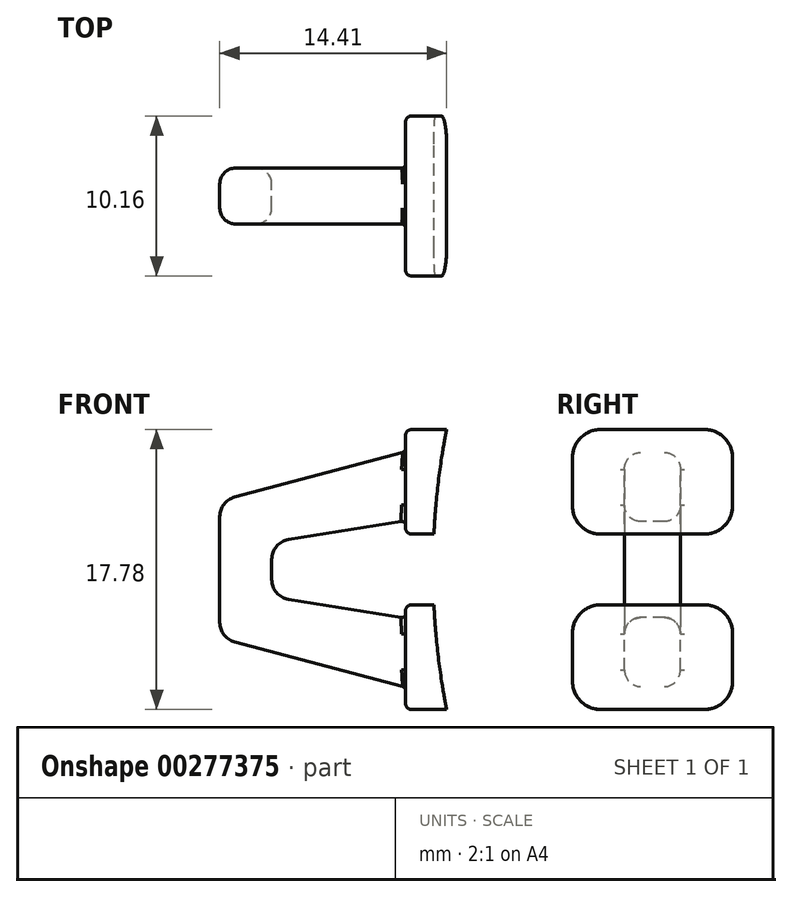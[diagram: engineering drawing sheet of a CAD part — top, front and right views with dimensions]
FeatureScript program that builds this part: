
annotation { "Feature Type Name" : "Feature", "Feature Type Description" : "" }
export const myFeature = defineFeature(function(context is Context, id is Id, definition is map)
    precondition{}
    {
        {
            var Q0;
            Q0=qCreatedBy(makeId("Front.planeOp"),FACE);
            var sketch = newSketch(context, id + "F0", { "sketchPlane" : qUnion([Q0])});
            skLineSegment(sketch, "E0", {"start": v(-28.89, -8.9) * mm, "end": v(-31.5, -8.9) * mm});
            skLineSegment(sketch, "E1", {"start": v(-31.5, -8.9) * mm, "end": v(-31.5, -7.48) * mm});
            skLineSegment(sketch, "E2.trimOffspring", {"start": v(-31.5, -3.1) * mm, "end": v(-31.5, -2.25) * mm});
            skLineSegment(sketch, "E3.MirrorCS", {"start": v(-31.5, 3.1) * mm, "end": v(-31.5, 2.25) * mm});
            skLineSegment(sketch, "E4.MirrorCS", {"start": v(-31.5, 8.9) * mm, "end": v(-31.5, 7.48) * mm});
            skLineSegment(sketch, "E5.MirrorCS", {"start": v(-28.89, 8.89) * mm, "end": v(-31.5, 8.89) * mm});
            skPoint(sketch, "E6.orphan", {"position": v(-29.04, 2.25) * mm});
            skPoint(sketch, "E7.orphan", {"position": v(-29.04, 8.9) * mm});
            skPoint(sketch, "E8.end.orphan", {"position": v(-29.04, -8.9) * mm});
            skPoint(sketch, "E8.start.orphan", {"position": v(-29.04, -2.25) * mm});
            skPoint(sketch, "E9.MirrorCS.end.orphan", {"position": v(-37.85, 0) * mm});
            skPoint(sketch, "E10.MirrorCS.end.orphan", {"position": v(-35.7, 0) * mm});
            skLineSegment(sketch, "E11", {"start": v(-31.5, -7.48) * mm, "end": v(-43.3, -4.35) * mm});
            skLineSegment(sketch, "E12", {"start": v(-43.3, -4.35) * mm, "end": v(-43.3, 0) * mm});
            skLineSegment(sketch, "E13", {"start": v(-40, 0) * mm, "end": v(-40, -1.73) * mm});
            skLineSegment(sketch, "E14", {"start": v(-40, -1.73) * mm, "end": v(-31.5, -3.1) * mm});
            skLineSegment(sketch, "E15.MirrorCS", {"start": v(-40, 0) * mm, "end": v(-40, 1.73) * mm});
            skLineSegment(sketch, "E16.MirrorCS", {"start": v(-43.3, 4.35) * mm, "end": v(-43.3, 0) * mm});
            skLineSegment(sketch, "E17.MirrorCS", {"start": v(-40, 1.73) * mm, "end": v(-31.5, 3.1) * mm});
            skLineSegment(sketch, "E18.MirrorCS", {"start": v(-31.5, 7.48) * mm, "end": v(-43.3, 4.35) * mm});
            skArc(sketch, "E19", {"start": v(-29.7, -2.25) * mm, "mid": v(-29.41, -5.58) * mm, "end": v(-28.89, -8.9) * mm});
            skLineSegment(sketch, "E20", {"start": v(-31.5, 2.25) * mm, "end": v(-29.7, 2.25) * mm});
            skLineSegment(sketch, "E21", {"start": v(-31.5, -2.25) * mm, "end": v(-29.7, -2.25) * mm});
            skArc(sketch, "E22.trimOffspring", {"start": v(-28.89, 8.9) * mm, "mid": v(-29.41, 5.58) * mm, "end": v(-29.7, 2.25) * mm});
            skSolve(sketch);
        }
        {
            var Q0;
            Q0=qSketchRegion(id+"F0",true);
            extrude(context, id + "F1", {"entities" : qUnion([Q0]), "depth" : 3.56 * mm, "symmetric" : true});
        }
        {
            var Q0;
            Q0=qCreatedBy(makeId("Front.planeOp"),FACE);
            var sketch = newSketch(context, id + "F2", { "sketchPlane" : qUnion([Q0])});
            skLineSegment(sketch, "E23.bottom", {"start": v(-31.5, 8.89) * mm, "end": v(-28.89, 8.89) * mm});
            skLineSegment(sketch, "E23.top", {"start": v(-31.5, -8.9) * mm, "end": v(-28.89, -8.9) * mm});
            skLineSegment(sketch, "E23.left", {"start": v(-31.5, 8.89) * mm, "end": v(-31.5, 2.25) * mm});
            skLineSegment(sketch, "E24.trimOffspring", {"start": v(-31.5, -2.25) * mm, "end": v(-31.5, -8.9) * mm});
            skArc(sketch, "E25", {"start": v(-29.7, -2.25) * mm, "mid": v(-29.41, -5.58) * mm, "end": v(-28.89, -8.9) * mm});
            skLineSegment(sketch, "E26", {"start": v(-31.5, 2.25) * mm, "end": v(-29.7, 2.25) * mm});
            skLineSegment(sketch, "E27", {"start": v(-31.5, -2.25) * mm, "end": v(-29.7, -2.25) * mm});
            skArc(sketch, "E28.trimOffspring", {"start": v(-28.89, 8.9) * mm, "mid": v(-29.41, 5.58) * mm, "end": v(-29.7, 2.25) * mm});
            skSolve(sketch);
        }
        {
            var Q0;
            Q0=qSketchRegion(id+"F2",true);
            extrude(context, id + "F3", {"entities" : qUnion([Q0]), "operationType" : NewBodyOperationType.ADD, "depth" : 10.16 * mm, "symmetric" : true});
        }
        {
            var Q0;
            Q0=makeQuery(id+"F3.opExtrude","CAP_EDGE",EDGE,{"disambiguationData":[OSD([sQuery(id+"F2.wireOp",EDGE,"E23.bottom")])],"isStart":false});
            var Q1;
            Q1=makeQuery(id+"F3.opExtrude","CAP_EDGE",EDGE,{"disambiguationData":[OSD([sQuery(id+"F2.wireOp",EDGE,"RXRbZ0R7-u3JN-APBt-SKa3-xy30dJVotsgh")])],"isStart":false});
            var Q2;
            Q2=makeQuery(id+"F3.opExtrude","CAP_EDGE",EDGE,{"disambiguationData":[OSD([sQuery(id+"F2.wireOp",EDGE,"E23.bottom")])],"isStart":true});
            var Q3;
            Q3=makeQuery(id+"F3.opExtrude","CAP_EDGE",EDGE,{"disambiguationData":[OSD([sQuery(id+"F2.wireOp",EDGE,"RXRbZ0R7-u3JN-APBt-SKa3-xy30dJVotsgh")])],"isStart":true});
            var Q4;
            Q4=makeQuery(id+"F3.opExtrude","CAP_EDGE",EDGE,{"disambiguationData":[OSD([sQuery(id+"F2.wireOp",EDGE,"TkA26Lc5-B4f9-dOkD-wxkU-3P7WS8GD69cp")])],"isStart":true});
            var Q5;
            Q5=makeQuery(id+"F3.opExtrude","CAP_EDGE",EDGE,{"disambiguationData":[OSD([sQuery(id+"F2.wireOp",EDGE,"E23.top")])],"isStart":true});
            var Q6;
            Q6=makeQuery(id+"F3.opExtrude","CAP_EDGE",EDGE,{"disambiguationData":[OSD([sQuery(id+"F2.wireOp",EDGE,"E23.top")])],"isStart":false});
            var Q7;
            Q7=makeQuery(id+"F3.opExtrude","CAP_EDGE",EDGE,{"disambiguationData":[OSD([sQuery(id+"F2.wireOp",EDGE,"TkA26Lc5-B4f9-dOkD-wxkU-3P7WS8GD69cp")])],"isStart":false});
            var Q8;
            Q8=makeQuery(id+"F3.opExtrude","CAP_EDGE",EDGE,{"disambiguationData":[OSD([sQuery(id+"F2.wireOp",EDGE,"E27")])],"isStart":false});
            var Q9;
            Q9=makeQuery(id+"F3.opExtrude","CAP_EDGE",EDGE,{"disambiguationData":[OSD([sQuery(id+"F2.wireOp",EDGE,"E26")])],"isStart":false});
            var Q10;
            Q10=makeQuery(id+"F3.opExtrude","CAP_EDGE",EDGE,{"disambiguationData":[OSD([sQuery(id+"F2.wireOp",EDGE,"E27")])],"isStart":true});
            var Q11;
            Q11=makeQuery(id+"F3.opExtrude","CAP_EDGE",EDGE,{"disambiguationData":[OSD([sQuery(id+"F2.wireOp",EDGE,"E26")])],"isStart":true});
            fillet(context, id + "F4", {"entities" : qUnion([Q0, Q1, Q2, Q3, Q4, Q5, Q6, Q7, Q8, Q9, Q10, Q11]), "radius" : 1.78 * mm, "tangentPropagation" : true, "allowEdgeOverflow" : false});
        }
        {
            var Q0;
            Q0=makeQuery(id+"F3.opExtrude","SWEPT_EDGE",EDGE,{"disambiguationData":[OSD([sQuery(id+"F2.wireOp",EDGE,"E23.left"),sQuery(id+"F2.wireOp",EDGE,"RXRbZ0R7-u3JN-APBt-SKa3-xy30dJVotsgh")])]});
            var Q1;
            Q1=makeQuery(id+"F4.opFillet","BLEND_EDGE",EDGE,{"blendedFrom":[makeQuery(id+"F3.opExtrude","CAP_EDGE",EDGE,{"disambiguationData":[OSD([sQuery(id+"F2.wireOp",EDGE,"RXRbZ0R7-u3JN-APBt-SKa3-xy30dJVotsgh")])],"isStart":true}),makeQuery(id+"F3.boolean.opBoolean","MERGE",FACE,{"derivedFrom":[makeQuery(id+"F1.opExtrude","SWEPT_FACE",FACE,{"disambiguationData":[OSD([sQuery(id+"F0.wireOp",EDGE,"E3.MirrorCS")])]}),makeQuery(id+"F1.opExtrude","SWEPT_FACE",FACE,{"disambiguationData":[OSD([sQuery(id+"F0.wireOp",EDGE,"E4.MirrorCS")])]}),makeQuery(id+"F3.opExtrude","SWEPT_FACE",FACE,{"disambiguationData":[OSD([sQuery(id+"F2.wireOp",EDGE,"E23.left")])]})]})],"blendedInto":[makeQuery(id+"F3.boolean.opBoolean","MERGE",FACE,{"derivedFrom":[makeQuery(id+"F1.opExtrude","SWEPT_FACE",FACE,{"disambiguationData":[OSD([sQuery(id+"F0.wireOp",EDGE,"E3.MirrorCS")])]}),makeQuery(id+"F1.opExtrude","SWEPT_FACE",FACE,{"disambiguationData":[OSD([sQuery(id+"F0.wireOp",EDGE,"E4.MirrorCS")])]}),makeQuery(id+"F3.opExtrude","SWEPT_FACE",FACE,{"disambiguationData":[OSD([sQuery(id+"F2.wireOp",EDGE,"E23.left")])]})]})]});
            var Q2;
            Q2=makeQuery(id+"F3.opExtrude","CAP_EDGE",EDGE,{"disambiguationData":[OSD([sQuery(id+"F2.wireOp",EDGE,"E23.left")])],"isStart":true});
            var Q3;
            Q3=makeQuery(id+"F4.opFillet","BLEND_EDGE",EDGE,{"blendedFrom":[makeQuery(id+"F3.opExtrude","CAP_EDGE",EDGE,{"disambiguationData":[OSD([sQuery(id+"F2.wireOp",EDGE,"E23.bottom")])],"isStart":true}),makeQuery(id+"F3.boolean.opBoolean","MERGE",FACE,{"derivedFrom":[makeQuery(id+"F1.opExtrude","SWEPT_FACE",FACE,{"disambiguationData":[OSD([sQuery(id+"F0.wireOp",EDGE,"E3.MirrorCS")])]}),makeQuery(id+"F1.opExtrude","SWEPT_FACE",FACE,{"disambiguationData":[OSD([sQuery(id+"F0.wireOp",EDGE,"E4.MirrorCS")])]}),makeQuery(id+"F3.opExtrude","SWEPT_FACE",FACE,{"disambiguationData":[OSD([sQuery(id+"F2.wireOp",EDGE,"E23.left")])]})]})],"blendedInto":[makeQuery(id+"F3.boolean.opBoolean","MERGE",FACE,{"derivedFrom":[makeQuery(id+"F1.opExtrude","SWEPT_FACE",FACE,{"disambiguationData":[OSD([sQuery(id+"F0.wireOp",EDGE,"E3.MirrorCS")])]}),makeQuery(id+"F1.opExtrude","SWEPT_FACE",FACE,{"disambiguationData":[OSD([sQuery(id+"F0.wireOp",EDGE,"E4.MirrorCS")])]}),makeQuery(id+"F3.opExtrude","SWEPT_FACE",FACE,{"disambiguationData":[OSD([sQuery(id+"F2.wireOp",EDGE,"E23.left")])]})]})]});
            var Q4;
            Q4=makeQuery(id+"F3.opExtrude","CAP_EDGE",EDGE,{"disambiguationData":[OSD([sQuery(id+"F2.wireOp",EDGE,"E23.left")])],"isStart":true});
            var Q5;
            Q5=makeQuery(id+"F3.boolean.opBoolean","MERGE",EDGE,{"derivedFrom":[makeQuery(id+"F1.opExtrude","SWEPT_EDGE",EDGE,{"disambiguationData":[OSD([sQuery(id+"F0.wireOp",EDGE,"E4.MirrorCS"),sQuery(id+"F0.wireOp",EDGE,"E5.MirrorCS")])]}),makeQuery(id+"F3.opExtrude","SWEPT_EDGE",EDGE,{"disambiguationData":[OSD([sQuery(id+"F2.wireOp",EDGE,"E23.bottom"),sQuery(id+"F2.wireOp",EDGE,"E23.left")])]})]});
            var Q6;
            Q6=makeQuery(id+"F3.opExtrude","SWEPT_EDGE",EDGE,{"disambiguationData":[OSD([sQuery(id+"F2.wireOp",EDGE,"TkA26Lc5-B4f9-dOkD-wxkU-3P7WS8GD69cp"),sQuery(id+"F2.wireOp",EDGE,"E24.trimOffspring")])]});
            fillet(context, id + "F5", {"entities" : qUnion([Q0, Q1, Q2, Q3, Q4, Q5, Q6]), "radius" : 0.38 * mm, "tangentPropagation" : true, "allowEdgeOverflow" : false});
        }
        {
            var Q0;
            Q0=makeQuery(id+"F1.opExtrude","SWEPT_EDGE",EDGE,{"disambiguationData":[OSD([sQuery(id+"F0.wireOp",EDGE,"E11"),sQuery(id+"F0.wireOp",EDGE,"E12")])]});
            var Q1;
            Q1=makeQuery(id+"F1.opExtrude","SWEPT_EDGE",EDGE,{"disambiguationData":[OSD([sQuery(id+"F0.wireOp",EDGE,"E16.MirrorCS"),sQuery(id+"F0.wireOp",EDGE,"E18.MirrorCS")])]});
            var Q2;
            Q2=makeQuery(id+"F1.opExtrude","SWEPT_EDGE",EDGE,{"disambiguationData":[OSD([sQuery(id+"F0.wireOp",EDGE,"E15.MirrorCS"),sQuery(id+"F0.wireOp",EDGE,"E17.MirrorCS")])]});
            var Q3;
            Q3=makeQuery(id+"F1.opExtrude","SWEPT_EDGE",EDGE,{"disambiguationData":[OSD([sQuery(id+"F0.wireOp",EDGE,"E13"),sQuery(id+"F0.wireOp",EDGE,"E14")])]});
            fillet(context, id + "F6", {"entities" : qUnion([Q0, Q1, Q2, Q3]), "radius" : 1.27 * mm, "tangentPropagation" : true, "allowEdgeOverflow" : false});
        }
        {
            var Q0;
            Q0=makeQuery(id+"F1.opExtrude","CAP_EDGE",EDGE,{"disambiguationData":[OSD([sQuery(id+"F0.wireOp",EDGE,"E11")])],"isStart":false});
            var Q1;
            Q1=makeQuery(id+"F1.opExtrude","CAP_EDGE",EDGE,{"disambiguationData":[OSD([sQuery(id+"F0.wireOp",EDGE,"E11")])],"isStart":true});
            var Q2;
            Q2=makeQuery(id+"F1.opExtrude","CAP_EDGE",EDGE,{"disambiguationData":[OSD([sQuery(id+"F0.wireOp",EDGE,"E13"),sQuery(id+"F0.wireOp",EDGE,"E15.MirrorCS")])],"isStart":false});
            var Q3;
            Q3=makeQuery(id+"F1.opExtrude","CAP_EDGE",EDGE,{"disambiguationData":[OSD([sQuery(id+"F0.wireOp",EDGE,"E17.MirrorCS")])],"isStart":true});
            fillet(context, id + "F7", {"entities" : qUnion([Q0, Q1, Q2, Q3]), "radius" : 1.02 * mm, "tangentPropagation" : true, "allowEdgeOverflow" : false});
        }
        {
            var Q0;
            Q0=makeQuery(id+"F3.boolean.opBoolean","INTERSECT",EDGE,{"derivedFrom":[makeQuery(id+"F1.opExtrude","CAP_FACE",FACE,{"disambiguationData":[OSD([sQuery(id+"F0.wireOp",EDGE,"E0"),sQuery(id+"F0.wireOp",EDGE,"E1"),sQuery(id+"F0.wireOp",EDGE,"beee627d-c7c4-4ff6-8b19-79b33334cd44"),sQuery(id+"F0.wireOp",EDGE,"E2.trimOffspring"),sQuery(id+"F0.wireOp",EDGE,"E3.MirrorCS"),sQuery(id+"F0.wireOp",EDGE,"E4.MirrorCS"),sQuery(id+"F0.wireOp",EDGE,"E5.MirrorCS"),sQuery(id+"F0.wireOp",EDGE,"684ba5a1-4310-4f21-9b21-088d0a01110c7.MirrorCS"),sQuery(id+"F0.wireOp",EDGE,"YPmfCHMG-XVIC-nbxh-loHK-GwVzSPm4SBvZ"),sQuery(id+"F0.wireOp",EDGE,"8e6f791d-0f4a-4d6e-afe4-d14939ce7773.trimOffspring"),sQuery(id+"F0.wireOp",EDGE,"E11"),sQuery(id+"F0.wireOp",EDGE,"E12"),sQuery(id+"F0.wireOp",EDGE,"E13"),sQuery(id+"F0.wireOp",EDGE,"E14"),sQuery(id+"F0.wireOp",EDGE,"E15.MirrorCS"),sQuery(id+"F0.wireOp",EDGE,"E16.MirrorCS"),sQuery(id+"F0.wireOp",EDGE,"E17.MirrorCS"),sQuery(id+"F0.wireOp",EDGE,"E18.MirrorCS")])],"isStart":false}),makeQuery(id+"F3.opExtrude","SWEPT_FACE",FACE,{"disambiguationData":[OSD([sQuery(id+"F2.wireOp",EDGE,"E24.trimOffspring")])]})]});
            var Q1;
            Q1=makeQuery(id+"F3.boolean.opBoolean","INTERSECT",EDGE,{"derivedFrom":[makeQuery(id+"F1.opExtrude","CAP_FACE",FACE,{"disambiguationData":[OSD([sQuery(id+"F0.wireOp",EDGE,"E0"),sQuery(id+"F0.wireOp",EDGE,"E1"),sQuery(id+"F0.wireOp",EDGE,"beee627d-c7c4-4ff6-8b19-79b33334cd44"),sQuery(id+"F0.wireOp",EDGE,"E2.trimOffspring"),sQuery(id+"F0.wireOp",EDGE,"E3.MirrorCS"),sQuery(id+"F0.wireOp",EDGE,"E4.MirrorCS"),sQuery(id+"F0.wireOp",EDGE,"E5.MirrorCS"),sQuery(id+"F0.wireOp",EDGE,"684ba5a1-4310-4f21-9b21-088d0a01110c7.MirrorCS"),sQuery(id+"F0.wireOp",EDGE,"YPmfCHMG-XVIC-nbxh-loHK-GwVzSPm4SBvZ"),sQuery(id+"F0.wireOp",EDGE,"8e6f791d-0f4a-4d6e-afe4-d14939ce7773.trimOffspring"),sQuery(id+"F0.wireOp",EDGE,"E11"),sQuery(id+"F0.wireOp",EDGE,"E12"),sQuery(id+"F0.wireOp",EDGE,"E13"),sQuery(id+"F0.wireOp",EDGE,"E14"),sQuery(id+"F0.wireOp",EDGE,"E15.MirrorCS"),sQuery(id+"F0.wireOp",EDGE,"E16.MirrorCS"),sQuery(id+"F0.wireOp",EDGE,"E17.MirrorCS"),sQuery(id+"F0.wireOp",EDGE,"E18.MirrorCS")])],"isStart":false}),makeQuery(id+"F3.opExtrude","SWEPT_FACE",FACE,{"disambiguationData":[OSD([sQuery(id+"F2.wireOp",EDGE,"E23.left")])]})]});
            fillet(context, id + "F8", {"entities" : qUnion([Q0, Q1]), "radius" : 0.25 * mm, "tangentPropagation" : true, "allowEdgeOverflow" : false});
        }
    });
